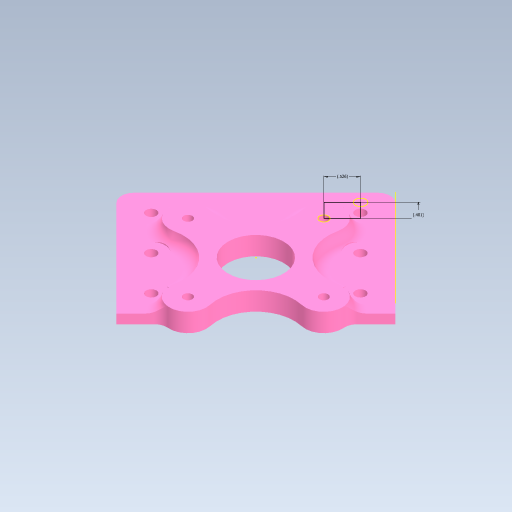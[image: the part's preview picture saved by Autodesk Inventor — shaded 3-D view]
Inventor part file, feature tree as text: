
AUTODESK INVENTOR PART (.ipt)
format: ipt  version: 2023 (Build 270158000, 158)  size: 316,928 bytes
history: native  units: in
note: dims shown in document units (in); Inventor stores cm internally (conversion verified against a paired STEP export)
features: sketch x5, extrude x4, projected_geometry x3, hole x1, fillet x1
ambient origin geometry x8: Origin, YZ Plane, XZ Plane, XY Plane, X Axis, Y Axis, Z Axis, Center Point
bodies: Solid1 (feature_tree)
feature tree (14):
  sketch  "Sketch1"  dims[d0=0.75in d1=1.5748in d3=360.0deg]
  extrude  "Extrusion1"  Depth=1.5748in TaperAngle=360.0deg
  hole  "Hole1"  [1 undecoded]
  extrude  "Extrusion2"  Depth=1.5748in TaperAngle=360.0deg
  fillet  "Fillet1"  Radius=0.375in
  extrude  "Extrusion3"  Depth=0.5in
  extrude  "Extrusion4"  Depth=0.25in
  sketch  "Sketch6"  dims[d22=4.0in d23=3.0in d24=0.5in d25=45.0deg d26=1.1811in d28=1.0in d29=0.7874in d31=3.0in d34=3.0in d35=1.125in d36=0.2087in d37=0.1875in d38=0.0in d39=0.25in d40=0.56in d41=0.56in d42=0.56in d43=0.56in d44=0.56in d45=0.56in d46=0.1875in d47=0.0in d49=0.0625in d50=0.0in d51=0.5in d52=0.125in d54=0.5256in d55=0.4006in]
  sketch  "Sketch2"  dims[d5=1.378in d6=1.125in]
  projected_geometry  "Projected Loop1"
  sketch  "Sketch3"  dims[d7=1.625in d8=1.5748in d10=360.0deg d12=0.375in d13=0.0in]
  projected_geometry  "Projected Loop2"
  sketch  "Sketch4"  dims[d14=0.1772in d15=0.75in d16=0.2067in d17=0.1969in d18=0.5635in d19=1.0in d20=0.8108in d21=0.5in]
  projected_geometry  "Projected Loop3"
note: 1 required parameter value undecoded (feature->parameter linkage not recoverable at this tier; creation-order binding heuristic only, values carry confidence <= 0.55)
